# Revit family: Recuperador_Calor_BAXI_SILA_RCT-MINI
name_source: partatom
category: Equipos mecánicos
units: mm (PartAtom-declared; Revit-internal decimal feet)

## family parameters
Anfitrión = Cara
Compartido = No
Corte con vacíos al cargar = No
Cota de conector redondo = Diámetro de uso
Mantener orientación de anotación = No
Número OmniClass = 23.75.70.00
Punto de cálculo de habitación = No
Tipo de pieza = Normal
Título OmniClass = HVAC Distribution Devices

## types (1)
- SILA RCT MINI
    AHS(average) Annual heating saved  [kWh primary energy/a] = 4646
    AHS(cold)   Annual heating saved  [kWh primary energy/a] = 9088
    AHS(warm)    Annual heating saved  [kWh primary energy/a] = 2101
    Absorbed Current max (A) = 0 A
    Absorbed Power max (W) = 79 W
    Airflow sensitivity to pressure variations at  ± 20 Pa = N.A.
    Annual electricity consumption (AEC) [kWh electricity/y] = 310
    Apparent Load = 0 VA
    Clean air outlet inside the room = Clean air outlet inside the room
    Connector description = Power supply
    Control factor CTRL = 0.65
    Control typology = Local.
    Declared ventilation type = UVR-B
    Difference of reference pressure = 50.0 Pa
    Drive type  (VM - VSD - N/A) = VM
    Edition number = 0
    Elevación por defecto = 1219 mm
    Energy classification = A
    Fabricante = BAXI
    Frequency (Hz) = 50 Hz
    Fresh air intake from outside = Fresh air intake from outside
    Indoor/outdoor air tightness [m3/h] = N.A.
    Intake from outside connexion diameter = 125 mm  [stored 0.410105 ft]
    Intake from outside flow = 0.0 m³/h
    Intake from room connexion diameter = 125 mm  [stored 0.410105 ft]
    Intake from room flow = 0.0 m³/h
    Main Material = Metal BAXI
    Max flow rate   (Qmax) = 103.0 m³/h
    Maximum external  leakage rates [%] = 5
    Maximum internal leakage rates (only for bidir.units) [%] = 5
    Mixing rate = N.A.
    Modelo = SILA RCT MINI
    Nominal height = 0
    Nominal width = 0
    Number of Poles = 1
    Outlet to outside connexion diameter = 125 mm  [stored 0.410105 ft]
    Outlet to outside flow = 0.0 m³/h
    Outlet to room connexion diameter = 125 mm  [stored 0.410105 ft]
    Outlet to room flow = 0.0 m³/h
    Position and description of visual filter warning = N.A.
    Power Factor = 0
    Power consumption of motorfans at Qmax = 79 W
    Reference flow rate = 72.0 m³/h
    SPI  (specific power input)  [W/(m3/h] = 0.5
    Sound Power level LWA ( at reference flow rate)  [dB(A)] = 42
    Stale air intake from room = Stale air intake from room
    Stale air outlet to outside = Stale air outlet to outside
    Thermal efficiency of heating recovery [%] = 87.7
    Typology of heating recovery system HRS = Heat recovery
    Voltage (V) = 230 V
    Weight Net (Kg) = 0

note: [stored X ft] marks values corroborated as IEEE doubles in the binary element streams (Revit-internal decimal feet)

## geometry (parser evidence)
native form markers: Sweep x3
no freeform markers — native parametric forms only
